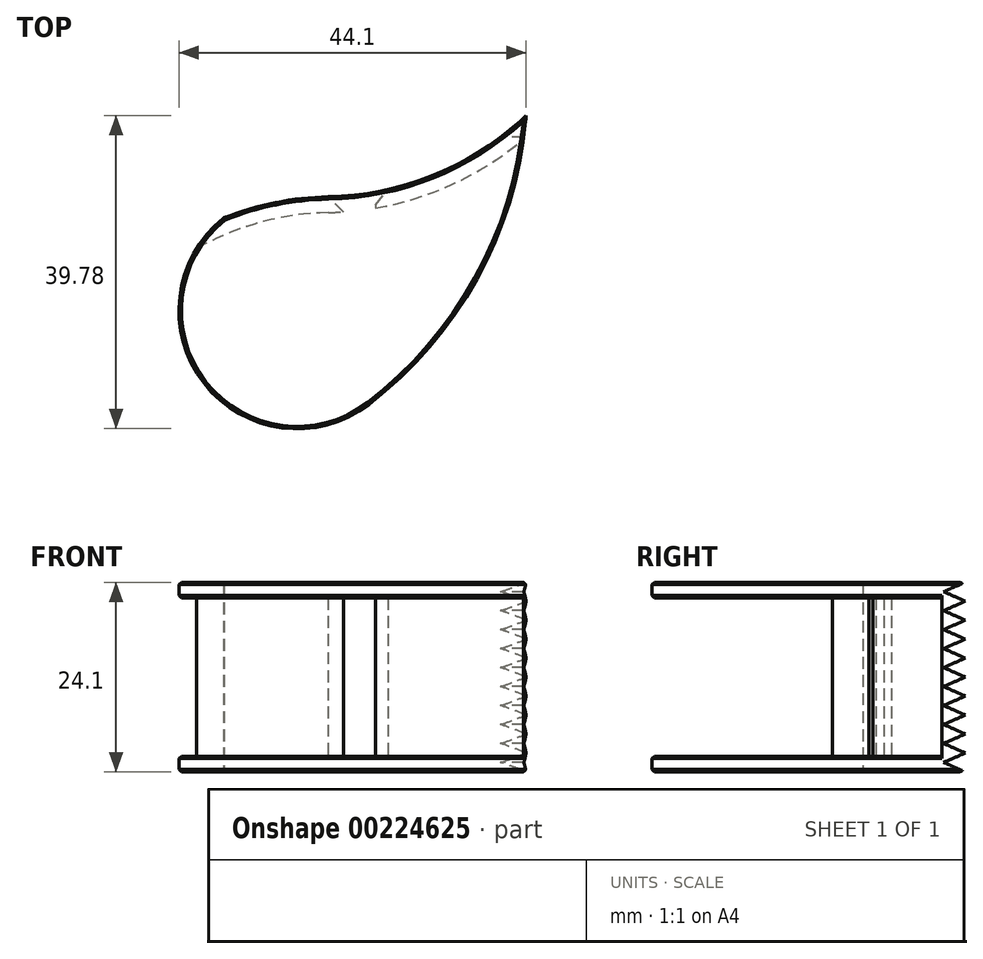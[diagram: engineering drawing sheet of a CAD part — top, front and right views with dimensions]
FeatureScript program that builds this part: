
annotation { "Feature Type Name" : "Feature", "Feature Type Description" : "" }
export const myFeature = defineFeature(function(context is Context, id is Id, definition is map)
    precondition{}
    {
        {
            assignVariable(context, id + "F0", {"name" : "PrintOffset", "anyValue" : 0.3});
        }
        {
            assignVariable(context, id + "F1", {"name" : "TapeWidth", "anyValue" : 19.5});
        }
        {
            assignVariable(context, id + "F2", {"name" : "WallThickness", "anyValue" : 2});
        }
        {
            assignVariable(context, id + "F3", {"name" : "TotalWidth", "anyValue" : (getVariable(context, 'TapeWidth') + (2 * getVariable(context, 'WallThickness')) + (2 * getVariable(context, 'PrintOffset'))) * mm});
        }
        {
            var Q0;
            Q0=qCreatedBy(makeId("Top.planeOp"),FACE);
            var sketch = newSketch(context, id + "F4", { "sketchPlane" : qUnion([Q0])});
            skArc(sketch, "E0", {"start": v(-0.7, 37.5) * mm, "mid": v(-10.28, -36.06) * mm, "end": v(20.36, 31.49) * mm});
            skArc(sketch, "E1", {"start": v(-0.7, 37.5) * mm, "mid": v(12.83, 40.3) * mm, "end": v(24.43, 47.8) * mm});
            skArc(sketch, "E2", {"start": v(-13.95, 34.8) * mm, "mid": v(-1.69, 8.33) * mm, "end": v(-0.7, 37.5) * mm});
            skArc(sketch, "E3", {"start": v(4.45, 11.12) * mm, "mid": v(18.34, 27.34) * mm, "end": v(24.43, 47.8) * mm});
            skSolve(sketch);
        }
        {
            var Q0;
            {var subQ0=sQuery(id+"F4.wireOp",EDGE,"E2");var subQ1=sQuery(id+"F4.wireOp",EDGE,"E0");var subQ3=makeQuery(id+"F4.imprint","INTERSECT",VERTEX,{"derivedFrom":[subQ1,subQ0]});Q0=makeQuery(id+"F4.imprint","IMPRINT",FACE,{"disambiguationData":[TD([[makeQuery(id+"F4.imprint","IMPRINT",EDGE,{"disambiguationData":[TD([[subQ3,-1.0]])],"derivedFrom":subQ0}),1.0]])]});}
            var Q1;
            {var subQ0=sQuery(id+"F4.wireOp",EDGE,"E1");Q1=makeQuery(id+"F4.imprint","IMPRINT",FACE,{"disambiguationData":[TD([[makeQuery(id+"F4.imprint","IMPRINT",EDGE,{"derivedFrom":subQ0}),-1.0]])]});}
            extrude(context, id + "F5", {"entities" : qUnion([Q0, Q1]), "depth" : getVariable(context, 'TotalWidth')});
        }
        {
            var Q0;
            Q0=makeQuery(id+"F5.opExtrude","SWEPT_FACE",FACE,{"disambiguationData":[OSD([sQuery(id+"F4.wireOp",EDGE,"E3")])]});
            var Q1;
            Q1=makeQuery(id+"F5.opExtrude","SWEPT_FACE",FACE,{"disambiguationData":[OSD([sQuery(id+"F4.wireOp",EDGE,"E2")])]});
            shell(context, id + "F6", {"entities" : qUnion([Q0, Q1]), "thickness" : (getVariable(context, 'WallThickness')) * mm});
        }
        {
            var Q0;
            Q0=qCreatedBy(makeId("Front.planeOp"),FACE);
            var sketch = newSketch(context, id + "F7", { "sketchPlane" : qUnion([Q0])});
            skLineSegment(sketch, "E4.0", {"start": v(24.43, 24.1) * mm, "end": v(24.43, 0) * mm, "construction": true});
            skLineSegment(sketch, "E4.1", {"start": v(-0.7, 24.1) * mm, "end": v(-0.7, 0) * mm, "construction": true});
            skLineSegment(sketch, "E4.2", {"start": v(-13.95, 24.1) * mm, "end": v(-13.95, 0) * mm, "construction": true});
            skLineSegment(sketch, "E5", {"start": v(-13.95, 24.1) * mm, "end": v(-0.7, 24.1) * mm, "construction": true});
            skLineSegment(sketch, "E6", {"start": v(-0.7, 0) * mm, "end": v(-13.95, 0) * mm, "construction": true});
            skLineSegment(sketch, "E7.1", {"start": v(1.3, 22.1) * mm, "end": v(5.3, 22.1) * mm});
            skLineSegment(sketch, "E7.2", {"start": v(1.3, 22.1) * mm, "end": v(1.3, 2) * mm});
            skLineSegment(sketch, "E7.3", {"start": v(5.3, 2) * mm, "end": v(1.3, 2) * mm});
            skLineSegment(sketch, "E8", {"start": v(5.3, 2) * mm, "end": v(5.3, 22.1) * mm});
            skSolve(sketch);
        }
        {
            var Q0;
            Q0=makeQuery(id+"F7.imprint","IMPRINT",FACE,{"disambiguationData":[TD([[makeQuery(id+"F7.imprint","IMPRINT",EDGE,{"derivedFrom":sQuery(id+"F7.wireOp",EDGE,"E7.1")}),-1.0]])]});
            extrude(context, id + "F8", {"entities" : qUnion([Q0]), "operationType" : NewBodyOperationType.REMOVE, "endBound" : BoundingType.THROUGH_ALL, "oppositeDirection" : true, "depth" : 25 * mm});
        }
        {
            var Q0;
            Q0=qCreatedBy(makeId("Right.planeOp"),FACE);
            var sketch = newSketch(context, id + "F9", { "sketchPlane" : qUnion([Q0])});
            skLineSegment(sketch, "E9.0", {"start": v(47.8, 24.1) * mm, "end": v(47.8, 0) * mm});
            skLineSegment(sketch, "E10", {"start": v(47.8, 0) * mm, "end": v(45.06, 1.2) * mm});
            skLineSegment(sketch, "E11", {"start": v(45.06, 1.2) * mm, "end": v(47.8, 2.41) * mm});
            skLineSegment(sketch, "E12.1.0.0", {"start": v(45.06, 3.62) * mm, "end": v(47.8, 4.82) * mm});
            skLineSegment(sketch, "E12.1.0.1", {"start": v(47.8, 2.41) * mm, "end": v(45.06, 3.62) * mm});
            skLineSegment(sketch, "E12.2.0.0", {"start": v(45.06, 6.03) * mm, "end": v(47.8, 7.23) * mm});
            skLineSegment(sketch, "E12.2.0.1", {"start": v(47.8, 4.82) * mm, "end": v(45.06, 6.03) * mm});
            skLineSegment(sketch, "E12.direction1", {"start": v(45.06, 1.2) * mm, "end": v(45.06, 3.62) * mm, "construction": true});
            skLineSegment(sketch, "E13.0.3.0", {"start": v(45.06, 8.44) * mm, "end": v(47.8, 9.64) * mm});
            skLineSegment(sketch, "E13.3.3.0", {"start": v(47.8, 7.23) * mm, "end": v(45.06, 8.44) * mm});
            skLineSegment(sketch, "E13.0.4.0", {"start": v(45.06, 10.85) * mm, "end": v(47.8, 12.05) * mm});
            skLineSegment(sketch, "E13.3.4.0", {"start": v(47.8, 9.64) * mm, "end": v(45.06, 10.85) * mm});
            skLineSegment(sketch, "E13.0.5.0", {"start": v(45.06, 13.26) * mm, "end": v(47.8, 14.46) * mm});
            skLineSegment(sketch, "E13.3.5.0", {"start": v(47.8, 12.05) * mm, "end": v(45.06, 13.26) * mm});
            skLineSegment(sketch, "E13.0.6.0", {"start": v(45.06, 15.67) * mm, "end": v(47.8, 16.87) * mm});
            skLineSegment(sketch, "E13.3.6.0", {"start": v(47.8, 14.46) * mm, "end": v(45.06, 15.67) * mm});
            skLineSegment(sketch, "E13.0.7.0", {"start": v(45.06, 18.08) * mm, "end": v(47.8, 19.28) * mm});
            skLineSegment(sketch, "E13.3.7.0", {"start": v(47.8, 16.87) * mm, "end": v(45.06, 18.08) * mm});
            skLineSegment(sketch, "E13.0.8.0", {"start": v(45.06, 20.49) * mm, "end": v(47.8, 21.7) * mm});
            skLineSegment(sketch, "E13.3.8.0", {"start": v(47.8, 19.28) * mm, "end": v(45.06, 20.48) * mm});
            skLineSegment(sketch, "E13.0.9.0", {"start": v(45.06, 22.9) * mm, "end": v(47.8, 24.1) * mm});
            skLineSegment(sketch, "E13.3.9.0", {"start": v(47.8, 21.7) * mm, "end": v(45.06, 22.9) * mm});
            skSolve(sketch);
        }
        {
            var Q0;
            Q0=qSketchRegion(id+"F9",true);
            var Q1;
            Q1=qConstructionFilter(qBodyType(qCreatedBy(id+"F9",EDGE),BodyType.WIRE),ConstructionObject.NO);
            extrude(context, id + "F10", {"entities" : qUnion([Q0]), "operationType" : NewBodyOperationType.REMOVE, "surfaceEntities" : qUnion([Q1]), "endBound" : BoundingType.THROUGH_ALL, "depth" : 25 * mm});
        }
        {
            var Q0;
            Q0=makeQuery(id+"F8.boolean.opBoolean","INTERSECT",EDGE,{"derivedFrom":[makeQuery(id+"F5.opExtrude","SWEPT_FACE",FACE,{"disambiguationData":[OSD([sQuery(id+"F4.wireOp",EDGE,"E1")])]}),makeQuery(id+"F8.opExtrude","SWEPT_FACE",FACE,{"disambiguationData":[OSD([sQuery(id+"F7.wireOp",EDGE,"E8")])]})]});
            var Q1;
            Q1=makeQuery(id+"F8.boolean.opBoolean","INTERSECT",EDGE,{"derivedFrom":[makeQuery(id+"F5.opExtrude","SWEPT_FACE",FACE,{"disambiguationData":[OSD([sQuery(id+"F4.wireOp",EDGE,"E1")])]}),makeQuery(id+"F8.opExtrude","SWEPT_FACE",FACE,{"disambiguationData":[OSD([sQuery(id+"F7.wireOp",EDGE,"E7.2")])]})]});
            chamfer(context, id + "F11", {"entities" : qUnion([Q0, Q1]), "width" : (getVariable(context, 'WallThickness')) * mm, "tangentPropagation" : true});
        }
        {
            var Q0;
            Q0=makeQuery(id+"F5.opExtrude","CAP_FACE",FACE,{"disambiguationData":[OSD([sQuery(id+"F4.wireOp",EDGE,"E0"),sQuery(id+"F4.wireOp",EDGE,"E1"),sQuery(id+"F4.wireOp",EDGE,"E2"),sQuery(id+"F4.wireOp",EDGE,"E3")])],"isStart":false});
            var Q1;
            Q1=makeQuery(id+"F5.opExtrude","CAP_FACE",FACE,{"disambiguationData":[OSD([sQuery(id+"F4.wireOp",EDGE,"E0"),sQuery(id+"F4.wireOp",EDGE,"E1"),sQuery(id+"F4.wireOp",EDGE,"E2"),sQuery(id+"F4.wireOp",EDGE,"E3")])],"isStart":true});
            var Q2;
            {var subQ0=sQuery(id+"F4.wireOp",EDGE,"E3");Q2=makeQuery(id+"F6.opShell","OFFSET_EDGE",EDGE,{"disambiguationData":[OSD([subQ0]),TDD([makeQuery(id+"F5.opExtrude","CAP_EDGE",EDGE,{"disambiguationData":[OSD([subQ0])],"isStart":true})])]});}
            var Q3;
            {var subQ0=sQuery(id+"F4.wireOp",EDGE,"E2");Q3=makeQuery(id+"F6.opShell","OFFSET_EDGE",EDGE,{"disambiguationData":[OSD([subQ0]),TDD([makeQuery(id+"F5.opExtrude","CAP_EDGE",EDGE,{"disambiguationData":[OSD([subQ0])],"isStart":true})])]});}
            var Q4;
            {var subQ0=sQuery(id+"F4.wireOp",EDGE,"E3");Q4=makeQuery(id+"F6.opShell","OFFSET_EDGE",EDGE,{"disambiguationData":[OSD([subQ0]),TDD([makeQuery(id+"F5.opExtrude","CAP_EDGE",EDGE,{"disambiguationData":[OSD([subQ0])],"isStart":false})])]});}
            var Q5;
            {var subQ0=sQuery(id+"F4.wireOp",EDGE,"E2");Q5=makeQuery(id+"F6.opShell","OFFSET_EDGE",EDGE,{"disambiguationData":[OSD([subQ0]),TDD([makeQuery(id+"F5.opExtrude","CAP_EDGE",EDGE,{"disambiguationData":[OSD([subQ0])],"isStart":false})])]});}
            var Q6;
            Q6=makeQuery(id+"F5.opExtrude","SWEPT_EDGE",EDGE,{"disambiguationData":[OSD([sQuery(id+"F4.wireOp",EDGE,"E0"),sQuery(id+"F4.wireOp",EDGE,"E2")])]});
            chamfer(context, id + "F12", {"entities" : qUnion([Q0, Q1, Q2, Q3, Q4, Q5, Q6]), "width" : (getVariable(context, 'PrintOffset')) * mm, "tangentPropagation" : true});
        }
    });
